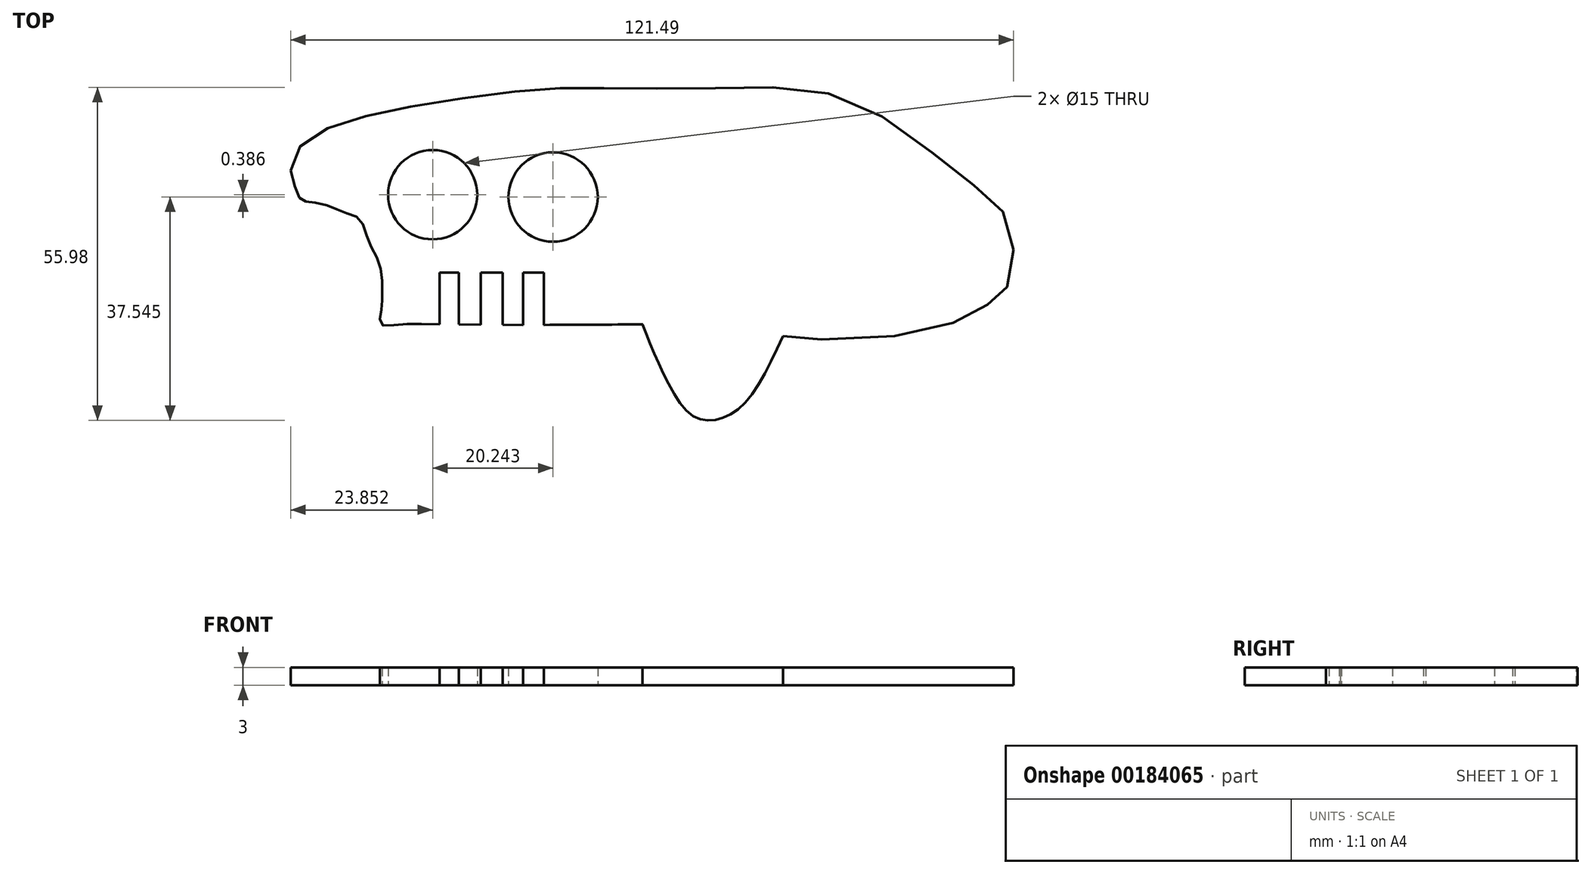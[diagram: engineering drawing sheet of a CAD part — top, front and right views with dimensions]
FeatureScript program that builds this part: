
annotation { "Feature Type Name" : "Feature", "Feature Type Description" : "" }
export const myFeature = defineFeature(function(context is Context, id is Id, definition is map)
    precondition{}
    {
        {
            var Q0;
            Q0=qCreatedBy(makeId("Top.planeOp"),FACE);
            var sketch = newSketch(context, id + "F0", { "sketchPlane" : qUnion([Q0])});
            skPoint(sketch, "E0.7.internal.snap0", {"position": v(-2.99, -21.54) * mm});
            skLineSegment(sketch, "E1", {"start": v(-56.72, 27.06) * mm, "end": v(-56.72, 27.06) * mm});
            skPoint(sketch, "E2.13.internal.orphan", {"position": v(-59, 26.12) * mm});
            skPoint(sketch, "E2.14.internal.orphan", {"position": v(-63.8, 20.53) * mm});
            skPoint(sketch, "E2.19.internal.orphan", {"position": v(-47.04, 0) * mm});
            skPoint(sketch, "E2.2.internal.orphan", {"position": v(46.65, -6.84) * mm});
            skPoint(sketch, "E2.20.internal.orphan", {"position": v(-47.04, -6.84) * mm});
            skPoint(sketch, "E2.21.internal.orphan", {"position": v(-40.48, -6.84) * mm});
            skPoint(sketch, "E3.1.internal.orphan", {"position": v(-56.16, 22.46) * mm});
            skPoint(sketch, "E3.2.internal.orphan", {"position": v(-56.16, 18.6) * mm});
            skFitSpline(sketch, "E4", {"points": [v(-65.49, 18.99) * mm, v(-63.8, 23.23) * mm, v(-56.72, 27.06) * mm, v(-43.95, 29.98) * mm, v(-25.83, 32.48) * mm, v(-12.91, 32.87) * mm, v(7.9, 32.87) * mm, v(28.73, 30.75) * mm, v(47.82, 17.64) * mm, v(55.14, 10.31) * mm, v(55.14, 0) * mm, v(51.87, -3.37) * mm, v(39.14, -8.39) * mm, v(17.24, -8.82) * mm, v(17.32, -8.66) * mm], "startDerivative": vector(20.8, 100.6) * mm, "endDerivative": vector(20.28, 19.04) * mm});
            skFitSpline(sketch, "E5", {"points": [v(-65.49, 18.99) * mm, v(-63.8, 14.17) * mm, v(-62.46, 13.78) * mm, v(-59, 13.01) * mm, v(-56.16, 11.86) * mm, v(-53.78, 10.7) * mm, v(-52.43, 7.23) * mm, v(-50.7, 3.76) * mm, v(-50.12, 0) * mm, v(-50.12, -2.6) * mm, v(-50.31, -4.92) * mm, v(-50.31, -6.84) * mm, v(-47.04, -6.84) * mm, v(-40.48, -6.84) * mm, v(-6.36, -6.84) * mm], "startDerivative": vector(19.42, -80.5) * mm, "endDerivative": vector(205.44, 1.36) * mm});
            skCircle(sketch, "E6", {"center": v(-41.64, 14.94) * mm, "radius": 7.5 * mm});
            skCircle(sketch, "E7", {"center": v(-21.4, 14.55) * mm, "radius": 7.5 * mm});
            skLineSegment(sketch, "E8.top", {"start": v(-40.48, 1.83) * mm, "end": v(-37.2, 1.83) * mm});
            skLineSegment(sketch, "E8.left", {"start": v(-40.48, -6.84) * mm, "end": v(-40.48, 1.83) * mm});
            skLineSegment(sketch, "E8.right", {"start": v(-37.2, -6.84) * mm, "end": v(-37.2, 1.83) * mm});
            skLineSegment(sketch, "E9.top", {"start": v(-33.54, 1.83) * mm, "end": v(-29.88, 1.83) * mm});
            skLineSegment(sketch, "E9.left", {"start": v(-33.54, -6.94) * mm, "end": v(-33.54, 1.83) * mm});
            skLineSegment(sketch, "E9.right", {"start": v(-29.88, -6.94) * mm, "end": v(-29.88, 1.83) * mm});
            skLineSegment(sketch, "E10.top", {"start": v(-26.4, 1.83) * mm, "end": v(-22.94, 1.83) * mm});
            skLineSegment(sketch, "E10.left", {"start": v(-26.4, -6.95) * mm, "end": v(-26.4, 1.83) * mm});
            skLineSegment(sketch, "E10.right", {"start": v(-22.94, -6.95) * mm, "end": v(-22.94, 1.83) * mm});
            skLineSegment(sketch, "E11", {"start": v(-37.2, -6.84) * mm, "end": v(-33.54, -6.94) * mm});
            skFitSpline(sketch, "E12.trimOffspring", {"points": [v(-65.49, 18.99) * mm, v(-63.8, 14.17) * mm, v(-62.46, 13.78) * mm, v(-59, 13.01) * mm, v(-56.16, 11.86) * mm, v(-53.78, 10.7) * mm, v(-52.43, 7.23) * mm, v(-50.7, 3.76) * mm, v(-50.12, 0) * mm, v(-50.12, -2.6) * mm, v(-50.31, -4.92) * mm, v(-50.31, -6.84) * mm, v(-47.04, -6.84) * mm, v(-40.48, -6.84) * mm, v(-6.36, -6.84) * mm], "startDerivative": vector(19.42, -80.5) * mm, "endDerivative": vector(205.44, 1.36) * mm});
            skLineSegment(sketch, "E13", {"start": v(-29.88, -6.94) * mm, "end": v(-26.4, -6.95) * mm});
            skFitSpline(sketch, "E14", {"points": [v(-6.36, -6.84) * mm, v(-2.98, -14.87) * mm, v(1.84, -22.03) * mm, v(6.04, -22.86) * mm, v(11.04, -19.8) * mm, v(17.24, -8.82) * mm], "startDerivative": vector(14.5, -36.97) * mm, "endDerivative": vector(22.97, 49.57) * mm});
            skSolve(sketch);
        }
        {
            var Q0;
            {var subQ0=sQuery(id+"F0.wireOp",EDGE,"E5");Q0=makeQuery(id+"F0.imprint","IMPRINT",FACE,{"disambiguationData":[TD([[makeQuery(id+"F0.imprint","IMPRINT",EDGE,{"derivedFrom":subQ0}),1.0]])]});}
            extrude(context, id + "F1", {"entities" : qUnion([Q0]), "depth" : 3 * mm});
        }
    });
